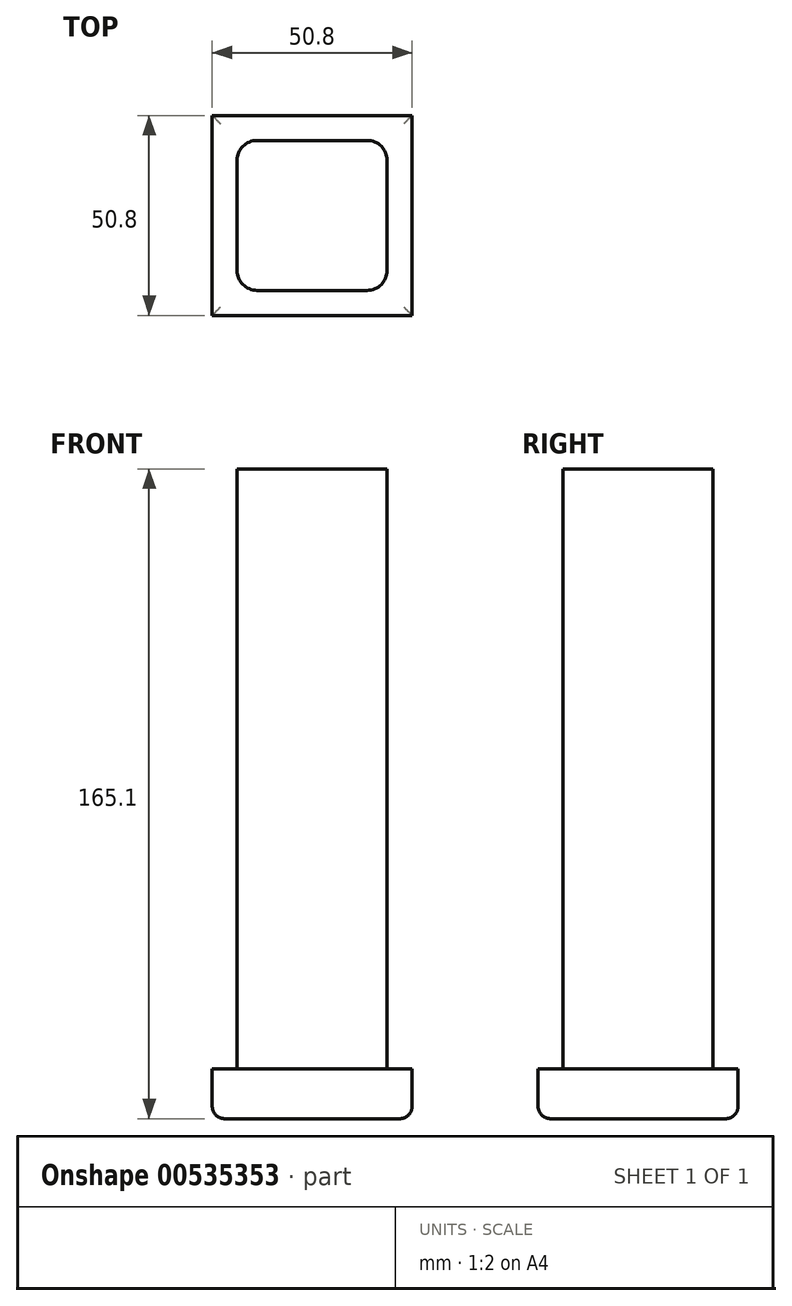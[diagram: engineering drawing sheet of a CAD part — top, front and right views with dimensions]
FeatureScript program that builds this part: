
annotation { "Feature Type Name" : "Feature", "Feature Type Description" : "" }
export const myFeature = defineFeature(function(context is Context, id is Id, definition is map)
    precondition{}
    {
        {
            var Q0;
            Q0=qCreatedBy(makeId("Top.planeOp"),FACE);
            var sketch = newSketch(context, id + "F0", { "sketchPlane" : qUnion([Q0])});
            skLineSegment(sketch, "E0.bottom", {"start": v(0, 0) * mm, "end": v(-50.8, 0) * mm});
            skLineSegment(sketch, "E0.top", {"start": v(0, 50.8) * mm, "end": v(-50.8, 50.8) * mm});
            skLineSegment(sketch, "E0.left", {"start": v(0, 0) * mm, "end": v(0, 50.8) * mm});
            skLineSegment(sketch, "E0.right", {"start": v(-50.8, 0) * mm, "end": v(-50.8, 50.8) * mm});
            skSolve(sketch);
        }
        {
            var Q0;
            Q0=makeQuery(id+"F0.imprint","IMPRINT",FACE,{"disambiguationData":[TD([[makeQuery(id+"F0.imprint","IMPRINT",EDGE,{"derivedFrom":sQuery(id+"F0.wireOp",EDGE,"E0.bottom")}),-1.0]])]});
            extrude(context, id + "F1", {"entities" : qUnion([Q0]), "depth" : 12.7 * mm, "offsetDistance" : 25.4 * mm});
        }
        {
            var Q0;
            Q0=makeQuery(id+"F1.opExtrude","CAP_FACE",FACE,{"disambiguationData":[OSD([sQuery(id+"F0.wireOp",EDGE,"E0.bottom"),sQuery(id+"F0.wireOp",EDGE,"E0.top"),sQuery(id+"F0.wireOp",EDGE,"E0.left"),sQuery(id+"F0.wireOp",EDGE,"E0.right")])],"isStart":false});
            var sketch = newSketch(context, id + "F2", { "sketchPlane" : qUnion([Q0])});
            skLineSegment(sketch, "E1.bottom", {"start": v(-44.45, 6.35) * mm, "end": v(-6.35, 6.35) * mm});
            skLineSegment(sketch, "E1.top", {"start": v(-44.45, 44.45) * mm, "end": v(-6.35, 44.45) * mm});
            skLineSegment(sketch, "E1.left", {"start": v(-44.45, 6.35) * mm, "end": v(-44.45, 44.45) * mm});
            skLineSegment(sketch, "E1.right", {"start": v(-6.35, 6.35) * mm, "end": v(-6.35, 44.45) * mm});
            skSolve(sketch);
        }
        {
            var Q0;
            Q0=makeQuery(id+"F2.imprint","IMPRINT",FACE,{"disambiguationData":[TD([[makeQuery(id+"F2.imprint","IMPRINT",EDGE,{"derivedFrom":sQuery(id+"F2.wireOp",EDGE,"E1.bottom")}),1.0]])]});
            extrude(context, id + "F3", {"entities" : qUnion([Q0]), "operationType" : NewBodyOperationType.ADD, "depth" : 152.4 * mm, "offsetDistance" : 25.4 * mm});
        }
        {
            var Q0;
            Q0=makeQuery(id+"F3.opExtrude","CAP_EDGE",EDGE,{"disambiguationData":[OSD([sQuery(id+"F2.wireOp",EDGE,"E1.bottom")])],"isStart":true});
            var Q1;
            Q1=makeQuery(id+"F3.opExtrude","CAP_EDGE",EDGE,{"disambiguationData":[OSD([sQuery(id+"F2.wireOp",EDGE,"E1.right")])],"isStart":true});
            var Q2;
            Q2=makeQuery(id+"F3.opExtrude","CAP_EDGE",EDGE,{"disambiguationData":[OSD([sQuery(id+"F2.wireOp",EDGE,"E1.top")])],"isStart":true});
            var Q3;
            Q3=makeQuery(id+"F3.opExtrude","CAP_EDGE",EDGE,{"disambiguationData":[OSD([sQuery(id+"F2.wireOp",EDGE,"E1.left")])],"isStart":true});
            var Q4;
            Q4=makeQuery(id+"F3.opExtrude","SWEPT_EDGE",EDGE,{"disambiguationData":[OSD([sQuery(id+"F2.wireOp",EDGE,"E1.top"),sQuery(id+"F2.wireOp",EDGE,"E1.left")])]});
            var Q5;
            Q5=makeQuery(id+"F3.opExtrude","SWEPT_EDGE",EDGE,{"disambiguationData":[OSD([sQuery(id+"F2.wireOp",EDGE,"E1.bottom"),sQuery(id+"F2.wireOp",EDGE,"E1.left")])]});
            var Q6;
            Q6=makeQuery(id+"F3.opExtrude","SWEPT_EDGE",EDGE,{"disambiguationData":[OSD([sQuery(id+"F2.wireOp",EDGE,"E1.bottom"),sQuery(id+"F2.wireOp",EDGE,"E1.right")])]});
            var Q7;
            Q7=makeQuery(id+"F3.opExtrude","SWEPT_EDGE",EDGE,{"disambiguationData":[OSD([sQuery(id+"F2.wireOp",EDGE,"E1.top"),sQuery(id+"F2.wireOp",EDGE,"E1.right")])]});
            fillet(context, id + "F4", {"entities" : qUnion([Q0, Q1, Q2, Q3, Q4, Q5, Q6, Q7]), "radius" : 5.08 * mm, "tangentPropagation" : true, "allowEdgeOverflow" : false});
        }
        {
            var Q0;
            Q0=makeQuery(id+"F1.opExtrude","CAP_FACE",FACE,{"disambiguationData":[OSD([sQuery(id+"F0.wireOp",EDGE,"E0.bottom"),sQuery(id+"F0.wireOp",EDGE,"E0.top"),sQuery(id+"F0.wireOp",EDGE,"E0.left"),sQuery(id+"F0.wireOp",EDGE,"E0.right")])],"isStart":true});
            fillet(context, id + "F5", {"entities" : qUnion([Q0]), "radius" : 3.17 * mm, "tangentPropagation" : true, "allowEdgeOverflow" : false});
        }
    });
